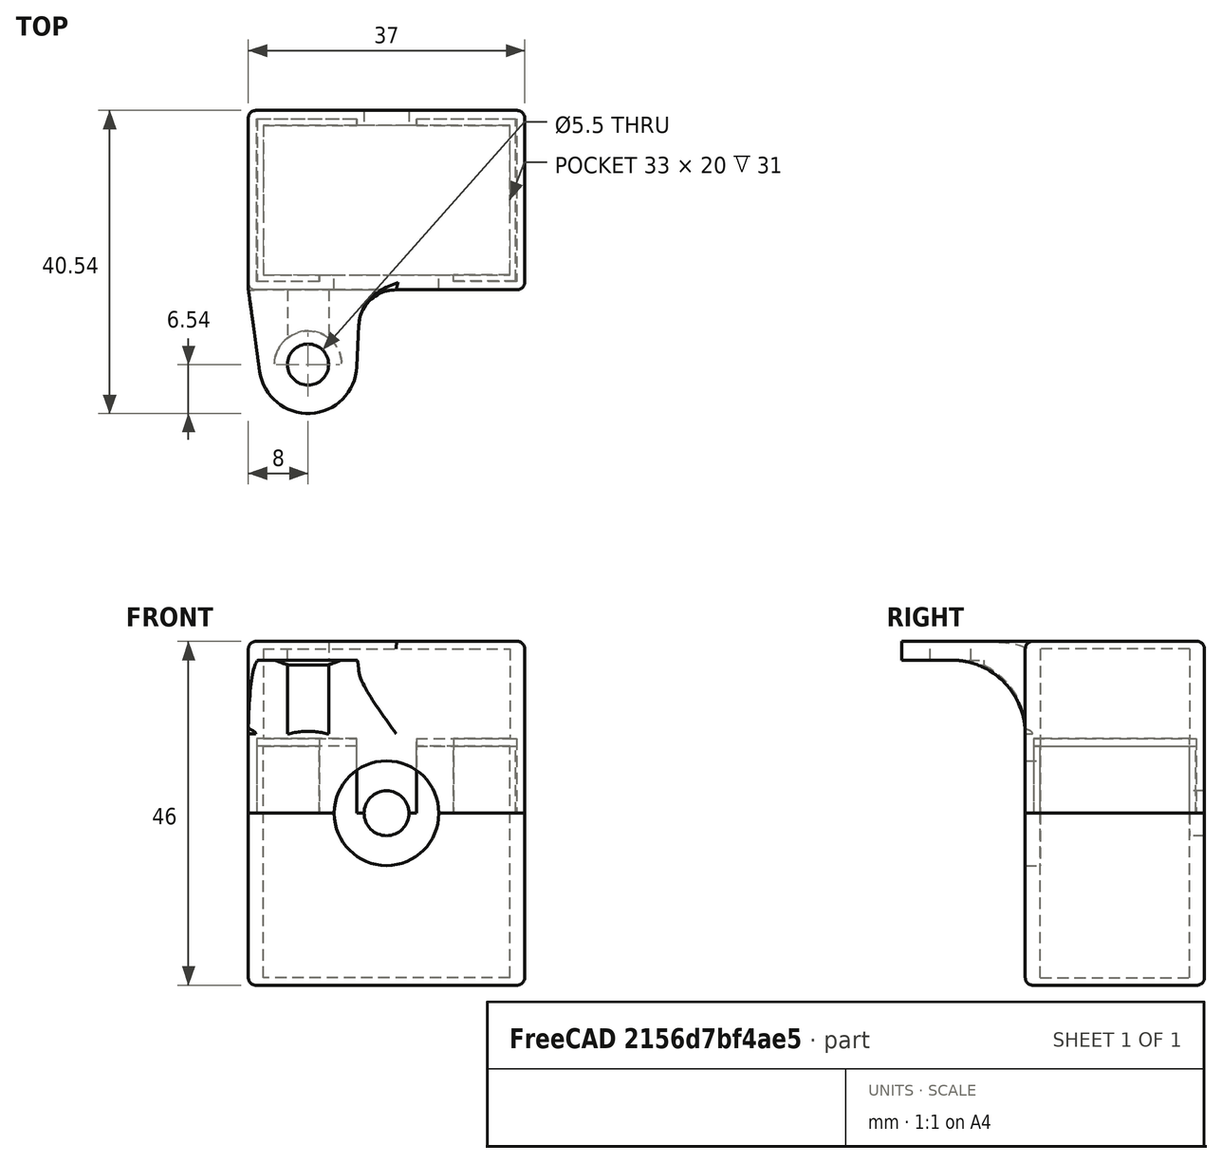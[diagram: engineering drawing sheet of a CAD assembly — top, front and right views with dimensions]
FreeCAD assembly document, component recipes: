
FREECAD ASSEMBLY — COMPONENT RECIPES ("logitech-quickcam-case")

This assembly document has 2 components, labeled P0..P1 below (a component is one placed body or linked part). 2 of them carry a construction recipe — the FreeCAD feature program that regenerates the part from scratch, quoted from this document or its linked companion documents; the rest are supplied as boundary geometry only. No exploded tour is included for this assembly.
COMPONENT P0 — recipe-attached ("free-side", modeled in this document).
Construction recipe (the document's own serialized feature program — sketch geometry with constraints, then the solid features built on it; lengths are millimeters unless a unit is written):

FEATURE [Sketcher::SketchObject] Sketch
  ArcFitTolerance = 1e-06
  AttachmentSupport = -> [Origin]
  ExternalTypes = [0]
  FullyConstrained = true
  MakeInternals = false
  MapMode = 5
  sketch-geometry (12):
    g0: LineSegment StartX=0 StartY=-24 StartZ=0 EndX=0 EndY=0 EndZ=0
    g1: LineSegment StartX=0 StartY=0 StartZ=0 EndX=37 EndY=0 EndZ=0
    g2: LineSegment StartX=37 StartY=0 StartZ=0 EndX=37 EndY=-24 EndZ=0
    g3: LineSegment StartX=37 StartY=-24 StartZ=0 EndX=0 EndY=-24 EndZ=0
    g4: LineSegment StartX=2 StartY=-22 StartZ=0 EndX=2 EndY=-2 EndZ=0
    g5: LineSegment StartX=2 StartY=-2 StartZ=0 EndX=35 EndY=-2 EndZ=0
    g6: LineSegment StartX=35 StartY=-2 StartZ=0 EndX=35 EndY=-22 EndZ=0
    g7: LineSegment StartX=35 StartY=-22 StartZ=0 EndX=2 EndY=-22 EndZ=0
    g8: LineSegment [constr] StartX=0 StartY=-2 StartZ=0 EndX=2 EndY=-2 EndZ=0
    g9: LineSegment [constr] StartX=35 StartY=-2 StartZ=0 EndX=37 EndY=-2 EndZ=0
    g10: LineSegment [constr] StartX=2 StartY=-22 StartZ=0 EndX=2 EndY=-24 EndZ=0
    g11: LineSegment [constr] StartX=2 StartY=-2 StartZ=0 EndX=2 EndY=0 EndZ=0
  constraints (36):
    c: Coincident(g0,g1)
    c: Coincident(g1,g2)
    c: Coincident(g2,g3)
    c: Coincident(g3,g0)
    c: Vertical(g0)
    c: Vertical(g2)
    c: Horizontal(g1)
    c: Horizontal(g3)
    c: PointOnObject(g0,g-2)
    c: PointOnObject(g1,g-1)
    c: Coincident(g4,g5)
    c: Coincident(g5,g6)
    c: Coincident(g6,g7)
    c: Coincident(g7,g4)
    c: Vertical(g4)
    c: Vertical(g6)
    c: Horizontal(g5)
    c: Horizontal(g7)
    c: PointOnObject(g8,g0)
    c: Coincident(g8,g4)
    c: Horizontal(g8)
    c: Coincident(g9,g5)
    c: PointOnObject(g9,g2)
    c: Horizontal(g9)
    c: Equal(g8,g9)
    c: Coincident(g10,g4)
    c: PointOnObject(g10,g3)
    c: Vertical(g10)
    c: Coincident(g11,g4)
    c: PointOnObject(g11,g1)
    c: Perpendicular(g11,g1)
    c: Equal(g11,g10)
    c: Equal(g11,g8)
    c: Distance(g4,g8) = 2
    c: DistanceY(g4,g4) = 20
    c: DistanceX(g7,g7) = 33
FEATURE [PartDesign::Pad] Pad
  Direction = (0,0,1)
  Length = 23
  Length2 = 10
  Profile = -> Sketch
  ReferenceAxis = -> Sketch [N_Axis]
  Refine = true
  SideType = 0
  Suppressed = false
  Type = 0
  Type2 = 0
FEATURE [Sketcher::SketchObject] Sketch001
  ArcFitTolerance = 1e-06
  AttachmentSupport = -> [Origin]
  ExternalTypes = [0]
  FullyConstrained = true
  MakeInternals = false
  MapMode = 5
  sketch-geometry (4):
    g0: LineSegment StartX=0 StartY=0 StartZ=0 EndX=0 EndY=-24 EndZ=0
    g1: LineSegment StartX=0 StartY=-24 StartZ=0 EndX=37 EndY=-24 EndZ=0
    g2: LineSegment StartX=37 StartY=-24 StartZ=0 EndX=37 EndY=0 EndZ=0
    g3: LineSegment StartX=37 StartY=0 StartZ=0 EndX=0 EndY=0 EndZ=0
  constraints (11):
    c: Coincident(g0,g1)
    c: Coincident(g1,g2)
    c: Coincident(g2,g3)
    c: Coincident(g3,g0)
    c: Vertical(g0)
    c: Vertical(g2)
    c: Horizontal(g1)
    c: Horizontal(g3)
    c: Distance(g0,g2) = 37
    c: Distance(g1,g3) = 24
    c: Coincident(g0,g-1)
FEATURE [PartDesign::Pad] Pad001
  BaseFeature = -> Pad
  Direction = (0,0,1)
  Length = 1
  Length2 = 10
  Profile = -> Sketch001
  ReferenceAxis = -> Sketch001 [N_Axis]
  Refine = true
  SideType = 0
  Suppressed = false
  Type = 0
  Type2 = 0
FEATURE [Sketcher::SketchObject] Sketch002
  ArcFitTolerance = 1e-06
  AttachmentSupport = -> [Origin]
  ExternalTypes = [0]
  FullyConstrained = true
  MakeInternals = false
  MapMode = 5
  sketch-geometry (28):
    g0: LineSegment StartX=1.2 StartY=-22.8 StartZ=0 EndX=1.2 EndY=-1.2 EndZ=0
    g1: LineSegment [constr] StartX=1.2 StartY=-1.2 StartZ=0 EndX=35.8 EndY=-1.2 EndZ=0
    g2: LineSegment StartX=35.8 StartY=-1.2 StartZ=0 EndX=35.8 EndY=-22.8 EndZ=0
    g3: LineSegment [constr] StartX=35.8 StartY=-22.8 StartZ=0 EndX=1.2 EndY=-22.8 EndZ=0
    g4: LineSegment StartX=2 StartY=-22 StartZ=0 EndX=2 EndY=-2 EndZ=0
    g5: LineSegment [constr] StartX=2 StartY=-2 StartZ=0 EndX=35 EndY=-2 EndZ=0
    g6: LineSegment StartX=35 StartY=-2 StartZ=0 EndX=35 EndY=-22 EndZ=0
    g7: LineSegment [constr] StartX=35 StartY=-22 StartZ=0 EndX=2 EndY=-22 EndZ=0
    g8: LineSegment [constr] StartX=1.2 StartY=-2 StartZ=0 EndX=2 EndY=-2 EndZ=0
    g9: LineSegment [constr] StartX=35 StartY=-2 StartZ=0 EndX=35.8 EndY=-2 EndZ=0
    g10: LineSegment [constr] StartX=2 StartY=-22 StartZ=0 EndX=2 EndY=-22.8 EndZ=0
    g11: LineSegment [constr] StartX=2 StartY=-2 StartZ=0 EndX=2 EndY=-1.2 EndZ=0
    g12: LineSegment [constr] StartX=1.2 StartY=-1.2 StartZ=0 EndX=0 EndY=-1.2 EndZ=0
    g13: LineSegment [constr] StartX=1.2 StartY=-1.2 StartZ=0 EndX=1.2 EndY=0 EndZ=0
    g14: LineSegment StartX=14.5 StartY=-2 StartZ=0 EndX=14.5 EndY=-1.2 EndZ=0
    g15: LineSegment StartX=22.5 StartY=-1.2 StartZ=0 EndX=22.5 EndY=-2 EndZ=0
    g16: LineSegment StartX=22.5 StartY=-1.2 StartZ=0 EndX=35.8 EndY=-1.2 EndZ=0
    g17: LineSegment StartX=35 StartY=-2 StartZ=0 EndX=22.5 EndY=-2 EndZ=0
    g18: LineSegment StartX=14.5 StartY=-2 StartZ=0 EndX=2 EndY=-2 EndZ=0
    g19: LineSegment StartX=14.5 StartY=-1.2 StartZ=0 EndX=2 EndY=-1.2 EndZ=0
    g20: LineSegment StartX=2 StartY=-1.2 StartZ=0 EndX=1.2 EndY=-1.2 EndZ=0
    g21: LineSegment StartX=2 StartY=-22 StartZ=0 EndX=9.5 EndY=-22 EndZ=0
    g22: LineSegment StartX=9.5 StartY=-22 StartZ=0 EndX=9.5 EndY=-22.8 EndZ=0
    g23: LineSegment StartX=9.5 StartY=-22.8 StartZ=0 EndX=1.2 EndY=-22.8 EndZ=0
    g24: LineSegment StartX=35 StartY=-22 StartZ=0 EndX=27.5 EndY=-22 EndZ=0
    g25: LineSegment StartX=27.5 StartY=-22 StartZ=0 EndX=27.5 EndY=-22.8 EndZ=0
    g26: LineSegment [constr] StartX=9.5 StartY=-22 StartZ=0 EndX=27.5 EndY=-22 EndZ=0
    g27: LineSegment StartX=27.5 StartY=-22.8 StartZ=0 EndX=35.8 EndY=-22.8 EndZ=0
  constraints (78):
    c: Coincident(g0,g1)
    c: Coincident(g1,g2)
    c: Coincident(g2,g3)
    c: Coincident(g3,g0)
    c: Vertical(g0)
    c: Vertical(g2)
    c: Horizontal(g1)
    c: Horizontal(g3)
    c: Coincident(g4,g5)
    c: Coincident(g5,g6)
    c: Coincident(g6,g7)
    c: Coincident(g7,g4)
    c: Vertical(g4)
    c: Vertical(g6)
    c: Horizontal(g5)
    c: Horizontal(g7)
    c: PointOnObject(g8,g0)
    c: Coincident(g8,g4)
    c: Horizontal(g8)
    c: Coincident(g9,g5)
    c: PointOnObject(g9,g2)
    c: Horizontal(g9)
    c: Equal(g8,g9)
    c: Coincident(g10,g4)
    c: PointOnObject(g10,g3)
    c: Vertical(g10)
    c: Coincident(g11,g4)
    c: PointOnObject(g11,g1)
    c: Perpendicular(g11,g1)
    c: Equal(g11,g10)
    c: Equal(g11,g8)
    c: Distance(g4,g8) = 0.8
    c: DistanceY(g4,g4) = 20
    c: DistanceX(g7,g7) = 33
    c: Coincident(g12,g0)
    c: PointOnObject(g12,g-2)
    c: Horizontal(g12)
    c: Coincident(g13,g0)
    c: Vertical(g13)
    c: Equal(g12,g13)
    c: PointOnObject(g13,g-1)
    c: DistanceY(g13,g13) = 1.2
    c: PointOnObject(g14,g5)
    c: PointOnObject(g14,g1)
    c: PointOnObject(g15,g1)
    c: PointOnObject(g15,g5)
    c: Vertical(g15)
    c: Coincident(g16,g15)
    c: Coincident(g16,g1)
    c: Coincident(g17,g5)
    c: Coincident(g17,g15)
    c: Coincident(g18,g14)
    c: Coincident(g18,g4)
    c: Coincident(g19,g14)
    c: Coincident(g19,g11)
    c: Perpendicular(g18,g14)
    c: DistanceX(g14,g15) = 8
    c: Coincident(g20,g11)
    c: Coincident(g20,g0)
    c: Coincident(g21,g4)
    c: Coincident(g21,g22)
    c: Vertical(g22)
    c: Coincident(g22,g23)
    c: Coincident(g23,g0)
    c: Coincident(g24,g6)
    c: Coincident(g24,g25)
    c: Coincident(g26,g21)
    c: Coincident(g26,g24)
    c: Horizontal(g26)
    c: DistanceX(g26,g26) = 18
    c: Perpendicular(g25,g24)
    c: Perpendicular(g6,g24)
    c: Horizontal(g25,g22)
    c: Horizontal(g22,g2)
    c: Equal(g18,g17)
    c: Equal(g21,g24)
    c: Coincident(g27,g25)
    c: Coincident(g27,g2)
FEATURE [Part::DatumPlane] DatumPlane
  AttachmentOffset = pos=(0,0,0) rot=(0,1,0;1.5708rad)
  AttachmentSupport = -> [Pad001]
  MapMode = 7
  Placement = pos=(2,-2,23) rot=(1,0,0;1.5708rad)
FEATURE [Sketcher::SketchObject] Sketch003
  ArcFitTolerance = 1e-06
  AttachmentSupport = -> [DatumPlane]
  ExternalTypes = [0]
  FullyConstrained = true
  MakeInternals = false
  MapMode = 5
  Placement = pos=(2,-2,23) rot=(1,0,0;1.5708rad)
  sketch-geometry (1):
    g0: Circle CenterX=16.5 CenterY=0 CenterZ=0 NormalX=0 NormalY=0 NormalZ=1 AngleXU=0 Radius=3
  constraints (3):
    c: PointOnObject(g0,g-1)
    c: Diameter(g0) = 6
    c: DistanceX(g-1,g0) = 16.5
FEATURE [PartDesign::Pocket] Pocket
  BaseFeature = -> Pad001
  Direction = (0,1,-2e-16)
  Length = 5
  Length2 = 5
  Profile = -> Sketch003
  ReferenceAxis = -> Sketch003 [N_Axis]
  Refine = true
  SideType = 2
  Suppressed = false
  Type = 0
  Type2 = 0
FEATURE [Part::DatumPlane] DatumPlane001
  AttachmentOffset = pos=(0,0,0) rot=(0,1,0;1.5708rad)
  AttachmentSupport = -> [Pad001]
  MapMode = 7
  Placement = pos=(35,-22,23) rot=(0,0.707107,0.707107;3.14159rad)
FEATURE [Sketcher::SketchObject] Sketch005
  ArcFitTolerance = 1e-06
  AttachmentSupport = -> [DatumPlane001]
  ExternalTypes = [0]
  FullyConstrained = true
  MakeInternals = false
  MapMode = 5
  Placement = pos=(35,-22,23) rot=(0,0.707107,0.707107;3.14159rad)
  sketch-geometry (1):
    g0: Circle CenterX=16.5 CenterY=0 CenterZ=0 NormalX=0 NormalY=0 NormalZ=1 AngleXU=0 Radius=7
  constraints (3):
    c: Diameter(g0) = 14
    c: PointOnObject(g0,g-1)
    c: DistanceX(g-1,g0) = 16.5
FEATURE [PartDesign::Pocket] Pocket001
  BaseFeature = -> Pocket
  Direction = (0,-1,2e-16)
  Length = 5
  Length2 = 5
  Profile = -> Sketch005
  ReferenceAxis = -> Sketch005 [N_Axis]
  Refine = true
  SideType = 2
  Suppressed = false
  Type = 0
  Type2 = 0
FEATURE [PartDesign::Pad] Pad002
  BaseFeature = -> Pocket001
  Direction = (0,0,1)
  Length = 32
  Length2 = 10
  Profile = -> Sketch002
  ReferenceAxis = -> Sketch002 [N_Axis]
  Refine = true
  SideType = 0
  Suppressed = false
  Type = 0
  Type2 = 0
FEATURE [PartDesign::Fillet] Fillet002
  Base = -> Pad002 [Edge29,Edge27,Edge28,Edge25,Edge49,Edge46,Edge26,Edge48]
  BaseFeature = -> Pad002
  Radius = 0.999
  Refine = true
  SupportTransform = false
  Suppressed = false
  UseAllEdges = false
FEATURE [PartDesign::Body] Body  label="free-side"
  AllowCompound = false
  Group = -> [Sketch,Pad,Sketch001,Pad001,Sketch003,Pocket,Sketch002,Sketch005,Pocket001,Pad002,DatumPlane,DatumPlane001,Fillet002]
  Origin = -> Origin
  Tip = -> Fillet002
COMPONENT P1 — recipe-attached ("bracket-side", modeled in this document).
Construction recipe (the document's own serialized feature program — sketch geometry with constraints, then the solid features built on it; lengths are millimeters unless a unit is written):

FEATURE [Sketcher::SketchObject] Sketch006
  ArcFitTolerance = 1e-06
  AttachmentOffset = pos=(0,0,0) rot=(1,0,0;3.14159rad)
  ExternalTypes = [0]
  FullyConstrained = true
  MakeInternals = false
  MapMode = 5
  Placement = pos=(0,0,23) rot=(0,0,1;0rad)
  sketch-geometry (28):
    g0: LineSegment StartX=1.1 StartY=-22.9 StartZ=0 EndX=1.1 EndY=-1.1 EndZ=0
    g1: LineSegment [constr] StartX=1.1 StartY=-1.1 StartZ=0 EndX=35.9 EndY=-1.1 EndZ=0
    g2: LineSegment StartX=35.9 StartY=-1.1 StartZ=0 EndX=35.9 EndY=-22.9 EndZ=0
    g3: LineSegment [constr] StartX=35.9 StartY=-22.9 StartZ=0 EndX=1.1 EndY=-22.9 EndZ=0
    g4: LineSegment StartX=2 StartY=-22 StartZ=0 EndX=2 EndY=-2 EndZ=0
    g5: LineSegment [constr] StartX=2 StartY=-2 StartZ=0 EndX=35 EndY=-2 EndZ=0
    g6: LineSegment StartX=35 StartY=-2 StartZ=0 EndX=35 EndY=-22 EndZ=0
    g7: LineSegment [constr] StartX=35 StartY=-22 StartZ=0 EndX=2 EndY=-22 EndZ=0
    g8: LineSegment [constr] StartX=1.1 StartY=-2 StartZ=0 EndX=2 EndY=-2 EndZ=0
    g9: LineSegment [constr] StartX=35 StartY=-2 StartZ=0 EndX=35.9 EndY=-2 EndZ=0
    g10: LineSegment [constr] StartX=2 StartY=-22 StartZ=0 EndX=2 EndY=-22.9 EndZ=0
    g11: LineSegment [constr] StartX=2 StartY=-2 StartZ=0 EndX=2 EndY=-1.1 EndZ=0
    g12: LineSegment [constr] StartX=1.1 StartY=-1.1 StartZ=0 EndX=0 EndY=-1.1 EndZ=0
    g13: LineSegment [constr] StartX=1.1 StartY=-1.1 StartZ=0 EndX=1.1 EndY=0 EndZ=0
    g14: LineSegment StartX=14.5 StartY=-2 StartZ=0 EndX=14.5 EndY=-1.1 EndZ=0
    g15: LineSegment StartX=22.5 StartY=-1.1 StartZ=0 EndX=22.5 EndY=-2 EndZ=0
    g16: LineSegment StartX=22.5 StartY=-1.1 StartZ=0 EndX=35.9 EndY=-1.1 EndZ=0
    g17: LineSegment StartX=35 StartY=-2 StartZ=0 EndX=22.5 EndY=-2 EndZ=0
    g18: LineSegment StartX=14.5 StartY=-2 StartZ=0 EndX=2 EndY=-2 EndZ=0
    g19: LineSegment StartX=14.5 StartY=-1.1 StartZ=0 EndX=2 EndY=-1.1 EndZ=0
    g20: LineSegment StartX=2 StartY=-1.1 StartZ=0 EndX=1.1 EndY=-1.1 EndZ=0
    g21: LineSegment StartX=2 StartY=-22 StartZ=0 EndX=9.5 EndY=-22 EndZ=0
    g22: LineSegment StartX=9.5 StartY=-22 StartZ=0 EndX=9.5 EndY=-22.9 EndZ=0
    g23: LineSegment StartX=9.5 StartY=-22.9 StartZ=0 EndX=1.1 EndY=-22.9 EndZ=0
    g24: LineSegment StartX=35 StartY=-22 StartZ=0 EndX=27.5 EndY=-22 EndZ=0
    g25: LineSegment StartX=27.5 StartY=-22 StartZ=0 EndX=27.5 EndY=-22.9 EndZ=0
    g26: LineSegment [constr] StartX=9.5 StartY=-22 StartZ=0 EndX=27.5 EndY=-22 EndZ=0
    g27: LineSegment StartX=27.5 StartY=-22.9 StartZ=0 EndX=35.9 EndY=-22.9 EndZ=0
  constraints (78):
    c: Coincident(g0,g1)
    c: Coincident(g1,g2)
    c: Coincident(g2,g3)
    c: Coincident(g3,g0)
    c: Vertical(g0)
    c: Vertical(g2)
    c: Horizontal(g1)
    c: Horizontal(g3)
    c: Coincident(g4,g5)
    c: Coincident(g5,g6)
    c: Coincident(g6,g7)
    c: Coincident(g7,g4)
    c: Vertical(g4)
    c: Vertical(g6)
    c: Horizontal(g5)
    c: Horizontal(g7)
    c: PointOnObject(g8,g0)
    c: Coincident(g8,g4)
    c: Horizontal(g8)
    c: Coincident(g9,g5)
    c: PointOnObject(g9,g2)
    c: Horizontal(g9)
    c: Equal(g8,g9)
    c: Coincident(g10,g4)
    c: PointOnObject(g10,g3)
    c: Vertical(g10)
    c: Coincident(g11,g4)
    c: PointOnObject(g11,g1)
    c: Perpendicular(g11,g1)
    c: Equal(g11,g10)
    c: Equal(g11,g8)
    c: Distance(g4,g8) = 0.9
    c: DistanceY(g4,g4) = 20
    c: DistanceX(g7,g7) = 33
    c: Coincident(g12,g0)
    c: PointOnObject(g12,g-2)
    c: Horizontal(g12)
    c: Coincident(g13,g0)
    c: Vertical(g13)
    c: Equal(g12,g13)
    c: PointOnObject(g13,g-1)
    c: DistanceY(g13,g13) = 1.1
    c: PointOnObject(g14,g5)
    c: PointOnObject(g14,g1)
    c: PointOnObject(g15,g1)
    c: PointOnObject(g15,g5)
    c: Vertical(g15)
    c: Coincident(g16,g15)
    c: Coincident(g16,g1)
    c: Coincident(g17,g5)
    c: Coincident(g17,g15)
    c: Coincident(g18,g14)
    c: Coincident(g18,g4)
    c: Coincident(g19,g14)
    c: Coincident(g19,g11)
    c: Perpendicular(g18,g14)
    c: DistanceX(g14,g15) = 8
    c: Coincident(g20,g11)
    c: Coincident(g20,g0)
    c: Coincident(g21,g4)
    c: Coincident(g21,g22)
    c: Vertical(g22)
    c: Coincident(g22,g23)
    c: Coincident(g23,g0)
    c: Coincident(g24,g6)
    c: Coincident(g24,g25)
    c: Coincident(g26,g21)
    c: Coincident(g26,g24)
    c: Horizontal(g26)
    c: DistanceX(g26,g26) = 18
    c: Perpendicular(g25,g24)
    c: Perpendicular(g6,g24)
    c: Horizontal(g25,g22)
    c: Horizontal(g22,g2)
    c: Equal(g18,g17)
    c: Equal(g21,g24)
    c: Coincident(g27,g25)
    c: Coincident(g27,g2)
FEATURE [Sketcher::SketchObject] Sketch007
  ArcFitTolerance = 1e-06
  AttachmentSupport = -> [Origin006]
  ExternalTypes = [0]
  FullyConstrained = true
  MakeInternals = false
  MapMode = 5
  sketch-geometry (12):
    g0: LineSegment StartX=0 StartY=-24 StartZ=0 EndX=0 EndY=0 EndZ=0
    g1: LineSegment StartX=0 StartY=0 StartZ=0 EndX=37 EndY=0 EndZ=0
    g2: LineSegment StartX=37 StartY=0 StartZ=0 EndX=37 EndY=-24 EndZ=0
    g3: LineSegment StartX=37 StartY=-24 StartZ=0 EndX=0 EndY=-24 EndZ=0
    g4: LineSegment StartX=2 StartY=-22 StartZ=0 EndX=2 EndY=-2 EndZ=0
    g5: LineSegment StartX=2 StartY=-2 StartZ=0 EndX=35 EndY=-2 EndZ=0
    g6: LineSegment StartX=35 StartY=-2 StartZ=0 EndX=35 EndY=-22 EndZ=0
    g7: LineSegment StartX=35 StartY=-22 StartZ=0 EndX=2 EndY=-22 EndZ=0
    g8: LineSegment [constr] StartX=0 StartY=-2 StartZ=0 EndX=2 EndY=-2 EndZ=0
    g9: LineSegment [constr] StartX=35 StartY=-2 StartZ=0 EndX=37 EndY=-2 EndZ=0
    g10: LineSegment [constr] StartX=2 StartY=-22 StartZ=0 EndX=2 EndY=-24 EndZ=0
    g11: LineSegment [constr] StartX=2 StartY=-2 StartZ=0 EndX=2 EndY=0 EndZ=0
  constraints (36):
    c: Coincident(g0,g1)
    c: Coincident(g1,g2)
    c: Coincident(g2,g3)
    c: Coincident(g3,g0)
    c: Vertical(g0)
    c: Vertical(g2)
    c: Horizontal(g1)
    c: Horizontal(g3)
    c: PointOnObject(g0,g-2)
    c: PointOnObject(g1,g-1)
    c: Coincident(g4,g5)
    c: Coincident(g5,g6)
    c: Coincident(g6,g7)
    c: Coincident(g7,g4)
    c: Vertical(g4)
    c: Vertical(g6)
    c: Horizontal(g5)
    c: Horizontal(g7)
    c: PointOnObject(g8,g0)
    c: Coincident(g8,g4)
    c: Horizontal(g8)
    c: Coincident(g9,g5)
    c: PointOnObject(g9,g2)
    c: Horizontal(g9)
    c: Equal(g8,g9)
    c: Coincident(g10,g4)
    c: PointOnObject(g10,g3)
    c: Vertical(g10)
    c: Coincident(g11,g4)
    c: PointOnObject(g11,g1)
    c: Perpendicular(g11,g1)
    c: Equal(g11,g10)
    c: Equal(g11,g8)
    c: Distance(g4,g8) = 2
    c: DistanceY(g4,g4) = 20
    c: DistanceX(g7,g7) = 33
FEATURE [PartDesign::Pad] Pad003
  Direction = (0,0,1)
  Length = 23
  Length2 = 10
  Profile = -> Sketch007
  ReferenceAxis = -> Sketch007 [N_Axis]
  Refine = true
  SideType = 0
  Suppressed = false
  Type = 0
  Type2 = 0
FEATURE [Sketcher::SketchObject] Sketch008
  ArcFitTolerance = 1e-06
  AttachmentSupport = -> [Origin006]
  ExternalTypes = [0]
  FullyConstrained = true
  MakeInternals = false
  MapMode = 5
  sketch-geometry (4):
    g0: LineSegment StartX=0 StartY=0 StartZ=0 EndX=0 EndY=-24 EndZ=0
    g1: LineSegment StartX=0 StartY=-24 StartZ=0 EndX=37 EndY=-24 EndZ=0
    g2: LineSegment StartX=37 StartY=-24 StartZ=0 EndX=37 EndY=0 EndZ=0
    g3: LineSegment StartX=37 StartY=0 StartZ=0 EndX=0 EndY=0 EndZ=0
  constraints (11):
    c: Coincident(g0,g1)
    c: Coincident(g1,g2)
    c: Coincident(g2,g3)
    c: Coincident(g3,g0)
    c: Vertical(g0)
    c: Vertical(g2)
    c: Horizontal(g1)
    c: Horizontal(g3)
    c: Distance(g0,g2) = 37
    c: Distance(g1,g3) = 24
    c: Coincident(g0,g-1)
FEATURE [PartDesign::Pad] Pad004
  BaseFeature = -> Pad003
  Direction = (0,0,1)
  Length = 1
  Length2 = 10
  Profile = -> Sketch008
  ReferenceAxis = -> Sketch008 [N_Axis]
  Refine = true
  SideType = 0
  Suppressed = false
  Type = 0
  Type2 = 0
FEATURE [Part::DatumPlane] DatumPlane002
  AttachmentOffset = pos=(0,0,0) rot=(0,1,0;1.5708rad)
  AttachmentSupport = -> [Pad004]
  MapMode = 7
  Placement = pos=(2,-2,23) rot=(1,0,0;1.5708rad)
FEATURE [Part::DatumPlane] DatumPlane003
  AttachmentOffset = pos=(0,0,0) rot=(0,1,0;1.5708rad)
  AttachmentSupport = -> [Pad004]
  MapMode = 7
  Placement = pos=(35,-22,23) rot=(0,0.707107,0.707107;3.14159rad)
FEATURE [Sketcher::SketchObject] Sketch009
  ArcFitTolerance = 1e-06
  AttachmentSupport = -> [Origin006]
  ExternalTypes = [0]
  FullyConstrained = true
  MakeInternals = false
  MapMode = 5
  sketch-geometry (28):
    g0: LineSegment StartX=1.2 StartY=-22.8 StartZ=0 EndX=1.2 EndY=-1.2 EndZ=0
    g1: LineSegment [constr] StartX=1.2 StartY=-1.2 StartZ=0 EndX=35.8 EndY=-1.2 EndZ=0
    g2: LineSegment StartX=35.8 StartY=-1.2 StartZ=0 EndX=35.8 EndY=-22.8 EndZ=0
    g3: LineSegment [constr] StartX=35.8 StartY=-22.8 StartZ=0 EndX=1.2 EndY=-22.8 EndZ=0
    g4: LineSegment StartX=2 StartY=-22 StartZ=0 EndX=2 EndY=-2 EndZ=0
    g5: LineSegment [constr] StartX=2 StartY=-2 StartZ=0 EndX=35 EndY=-2 EndZ=0
    g6: LineSegment StartX=35 StartY=-2 StartZ=0 EndX=35 EndY=-22 EndZ=0
    g7: LineSegment [constr] StartX=35 StartY=-22 StartZ=0 EndX=2 EndY=-22 EndZ=0
    g8: LineSegment [constr] StartX=1.2 StartY=-2 StartZ=0 EndX=2 EndY=-2 EndZ=0
    g9: LineSegment [constr] StartX=35 StartY=-2 StartZ=0 EndX=35.8 EndY=-2 EndZ=0
    g10: LineSegment [constr] StartX=2 StartY=-22 StartZ=0 EndX=2 EndY=-22.8 EndZ=0
    g11: LineSegment [constr] StartX=2 StartY=-2 StartZ=0 EndX=2 EndY=-1.2 EndZ=0
    g12: LineSegment [constr] StartX=1.2 StartY=-1.2 StartZ=0 EndX=0 EndY=-1.2 EndZ=0
    g13: LineSegment [constr] StartX=1.2 StartY=-1.2 StartZ=0 EndX=1.2 EndY=0 EndZ=0
    g14: LineSegment StartX=14.5 StartY=-2 StartZ=0 EndX=14.5 EndY=-1.2 EndZ=0
    g15: LineSegment StartX=22.5 StartY=-1.2 StartZ=0 EndX=22.5 EndY=-2 EndZ=0
    g16: LineSegment StartX=22.5 StartY=-1.2 StartZ=0 EndX=35.8 EndY=-1.2 EndZ=0
    g17: LineSegment StartX=35 StartY=-2 StartZ=0 EndX=22.5 EndY=-2 EndZ=0
    g18: LineSegment StartX=14.5 StartY=-2 StartZ=0 EndX=2 EndY=-2 EndZ=0
    g19: LineSegment StartX=14.5 StartY=-1.2 StartZ=0 EndX=2 EndY=-1.2 EndZ=0
    g20: LineSegment StartX=2 StartY=-1.2 StartZ=0 EndX=1.2 EndY=-1.2 EndZ=0
    g21: LineSegment StartX=2 StartY=-22 StartZ=0 EndX=9.5 EndY=-22 EndZ=0
    g22: LineSegment StartX=9.5 StartY=-22 StartZ=0 EndX=9.5 EndY=-22.8 EndZ=0
    g23: LineSegment StartX=9.5 StartY=-22.8 StartZ=0 EndX=1.2 EndY=-22.8 EndZ=0
    g24: LineSegment StartX=35 StartY=-22 StartZ=0 EndX=27.5 EndY=-22 EndZ=0
    g25: LineSegment StartX=27.5 StartY=-22 StartZ=0 EndX=27.5 EndY=-22.8 EndZ=0
    g26: LineSegment [constr] StartX=9.5 StartY=-22 StartZ=0 EndX=27.5 EndY=-22 EndZ=0
    g27: LineSegment StartX=27.5 StartY=-22.8 StartZ=0 EndX=35.8 EndY=-22.8 EndZ=0
  constraints (78):
    c: Coincident(g0,g1)
    c: Coincident(g1,g2)
    c: Coincident(g2,g3)
    c: Coincident(g3,g0)
    c: Vertical(g0)
    c: Vertical(g2)
    c: Horizontal(g1)
    c: Horizontal(g3)
    c: Coincident(g4,g5)
    c: Coincident(g5,g6)
    c: Coincident(g6,g7)
    c: Coincident(g7,g4)
    c: Vertical(g4)
    c: Vertical(g6)
    c: Horizontal(g5)
    c: Horizontal(g7)
    c: PointOnObject(g8,g0)
    c: Coincident(g8,g4)
    c: Horizontal(g8)
    c: Coincident(g9,g5)
    c: PointOnObject(g9,g2)
    c: Horizontal(g9)
    c: Equal(g8,g9)
    c: Coincident(g10,g4)
    c: PointOnObject(g10,g3)
    c: Vertical(g10)
    c: Coincident(g11,g4)
    c: PointOnObject(g11,g1)
    c: Perpendicular(g11,g1)
    c: Equal(g11,g10)
    c: Equal(g11,g8)
    c: Distance(g4,g8) = 0.8
    c: DistanceY(g4,g4) = 20
    c: DistanceX(g7,g7) = 33
    c: Coincident(g12,g0)
    c: PointOnObject(g12,g-2)
    c: Horizontal(g12)
    c: Coincident(g13,g0)
    c: Vertical(g13)
    c: Equal(g12,g13)
    c: PointOnObject(g13,g-1)
    c: DistanceY(g13,g13) = 1.2
    c: PointOnObject(g14,g5)
    c: PointOnObject(g14,g1)
    c: PointOnObject(g15,g1)
    c: PointOnObject(g15,g5)
    c: Vertical(g15)
    c: Coincident(g16,g15)
    c: Coincident(g16,g1)
    c: Coincident(g17,g5)
    c: Coincident(g17,g15)
    c: Coincident(g18,g14)
    c: Coincident(g18,g4)
    c: Coincident(g19,g14)
    c: Coincident(g19,g11)
    c: Perpendicular(g18,g14)
    c: DistanceX(g14,g15) = 8
    c: Coincident(g20,g11)
    c: Coincident(g20,g0)
    c: Coincident(g21,g4)
    c: Coincident(g21,g22)
    c: Vertical(g22)
    c: Coincident(g22,g23)
    c: Coincident(g23,g0)
    c: Coincident(g24,g6)
    c: Coincident(g24,g25)
    c: Coincident(g26,g21)
    c: Coincident(g26,g24)
    c: Horizontal(g26)
    c: DistanceX(g26,g26) = 18
    c: Perpendicular(g25,g24)
    c: Perpendicular(g6,g24)
    c: Horizontal(g25,g22)
    c: Horizontal(g22,g2)
    c: Equal(g18,g17)
    c: Equal(g21,g24)
    c: Coincident(g27,g25)
    c: Coincident(g27,g2)
FEATURE [Sketcher::SketchObject] Sketch010
  ArcFitTolerance = 1e-06
  AttachmentSupport = -> [DatumPlane002]
  ExternalTypes = [0]
  FullyConstrained = true
  MakeInternals = false
  MapMode = 5
  Placement = pos=(2,-2,23) rot=(1,0,0;1.5708rad)
  sketch-geometry (1):
    g0: Circle CenterX=16.5 CenterY=0 CenterZ=0 NormalX=0 NormalY=0 NormalZ=1 AngleXU=0 Radius=3
  constraints (3):
    c: PointOnObject(g0,g-1)
    c: Diameter(g0) = 6
    c: DistanceX(g-1,g0) = 16.5
FEATURE [PartDesign::Pocket] Pocket002
  BaseFeature = -> Pad004
  Direction = (0,1,-2e-16)
  Length = 5
  Length2 = 5
  Profile = -> Sketch010
  ReferenceAxis = -> Sketch010 [N_Axis]
  Refine = true
  SideType = 2
  Suppressed = false
  Type = 0
  Type2 = 0
FEATURE [Sketcher::SketchObject] Sketch011
  ArcFitTolerance = 1e-06
  AttachmentSupport = -> [DatumPlane003]
  ExternalTypes = [0]
  FullyConstrained = true
  MakeInternals = false
  MapMode = 5
  Placement = pos=(35,-22,23) rot=(0,0.707107,0.707107;3.14159rad)
  sketch-geometry (1):
    g0: Circle CenterX=16.5 CenterY=0 CenterZ=0 NormalX=0 NormalY=0 NormalZ=1 AngleXU=0 Radius=7
  constraints (3):
    c: Diameter(g0) = 14
    c: PointOnObject(g0,g-1)
    c: DistanceX(g-1,g0) = 16.5
FEATURE [PartDesign::Pocket] Pocket003
  BaseFeature = -> Pocket002
  Direction = (0,-1,2e-16)
  Length = 5
  Length2 = 5
  Profile = -> Sketch011
  ReferenceAxis = -> Sketch011 [N_Axis]
  Refine = true
  SideType = 2
  Suppressed = false
  Type = 0
  Type2 = 0
FEATURE [PartDesign::Pad] Pad005
  BaseFeature = -> Pocket003
  Direction = (0,0,1)
  Length = 27
  Length2 = 10
  Profile = -> Sketch009
  ReferenceAxis = -> Sketch009 [N_Axis]
  Refine = true
  SideType = 0
  Suppressed = false
  Type = 0
  Type2 = 0
FEATURE [PartDesign::Pocket] Pocket004
  BaseFeature = -> Pad005
  Direction = (0,0,-1)
  Length = 10
  Length2 = 5
  Profile = -> Sketch006
  ReferenceAxis = -> Sketch006 [N_Axis]
  Refine = true
  SideType = 2
  Suppressed = false
  Type = 0
  Type2 = 0
FEATURE [Part::DatumPlane] DatumPlane005
  AttachmentOffset = pos=(0,0,0) rot=(-0.57735,0.57735,0.57735;2.0944rad)
  AttachmentSupport = -> [Pocket004]
  MapMode = 7
  Placement = pos=(37,-24,0) rot=(0,0,1;3.14159rad)
FEATURE [Sketcher::SketchObject] Sketch013
  ArcFitTolerance = 1e-06
  AttachmentSupport = -> [DatumPlane005]
  ExternalTypes = [0]
  FullyConstrained = true
  MakeInternals = false
  MapMode = 5
  Placement = pos=(37,-24,0) rot=(0,0,1;3.14159rad)
  sketch-geometry (7):
    g0: ArcOfCircle CenterX=8 CenterY=10 CenterZ=0 NormalX=0 NormalY=0 NormalZ=1 AngleXU=0 Radius=6.53503 StartAngle=0.0457794 EndAngle=3.00239
    g1: Circle CenterX=8 CenterY=10 CenterZ=0 NormalX=0 NormalY=0 NormalZ=1 AngleXU=0 Radius=2.75
    g2: LineSegment StartX=1.52819 StartY=10.9068 StartZ=0 EndX=-2e-16 EndY=0 EndZ=0
    g3: LineSegment StartX=14.5282 StartY=10.2991 StartZ=0 EndX=15 EndY=0 EndZ=0
    g4: LineSegment StartX=-2e-16 StartY=0 StartZ=0 EndX=15 EndY=0 EndZ=0
    g5: LineSegment [constr] StartX=1.52819 StartY=10.9068 StartZ=0 EndX=11.304 EndY=80.6778 EndZ=0
    g6: LineSegment [constr] StartX=14.5282 StartY=10.2991 StartZ=0 EndX=11.304 EndY=80.6778 EndZ=0
  constraints (17):
    c: Coincident(g1,g0)
    c: Diameter(g1) = 5.5
    c: DistanceX(g0,g0) = 13
    c: Coincident(g2,g0)
    c: Coincident(g3,g0)
    c: PointOnObject(g3,g-1)
    c: Coincident(g4,g2)
    c: Coincident(g4,g3)
    c: Distance(g0,g-2) = 8
    c: Coincident(g2,g-1)
    c: Distance(g0,g-1) = 10
    c: Tangent(g6,g0) = -1.5708
    c: Parallel(g6,g3)
    c: Parallel(g2,g5)
    c: Tangent(g5,g0) = 1.5708
    c: DistanceX(g4,g4) = 15
    c: Coincident(g5,g6)
FEATURE [PartDesign::Pad] Pad006
  BaseFeature = -> Pocket004
  Direction = (0,0,1)
  Length = 2.5
  Length2 = 10
  Profile = -> Sketch013
  ReferenceAxis = -> Sketch013 [N_Axis]
  Refine = true
  SideType = 0
  Suppressed = false
  Type = 0
  Type2 = 0
FEATURE [PartDesign::Fillet] Fillet
  Base = -> Pad006 [Edge70]
  BaseFeature = -> Pad006
  Radius = 9.9
  Refine = true
  SupportTransform = false
  Suppressed = false
  UseAllEdges = false
FEATURE [PartDesign::Fillet] Fillet003
  Base = -> Fillet [Edge1,Edge16,Edge15,Edge51,Edge11,Edge9,Edge50,Edge49]
  BaseFeature = -> Fillet
  Radius = 1
  Refine = true
  SupportTransform = false
  Suppressed = false
  UseAllEdges = false
FEATURE [PartDesign::Fillet] Fillet004
  Base = -> Fillet003 [Edge7]
  BaseFeature = -> Fillet003
  Radius = 5
  Refine = true
  SupportTransform = false
  Suppressed = false
  UseAllEdges = false
FEATURE [Sketcher::SketchObject] Sketch014
  ArcFitTolerance = 1e-06
  AttachmentOffset = pos=(0,0,2.5) rot=(0,0,1;0rad)
  AttachmentSupport = -> [DatumPlane005]
  ExternalTypes = [0]
  FullyConstrained = true
  MakeInternals = false
  MapMode = 5
  Placement = pos=(37,-24,2.5) rot=(0,0,1;3.14159rad)
  sketch-geometry (1):
    g0: Circle CenterX=8 CenterY=10 CenterZ=0 NormalX=0 NormalY=0 NormalZ=1 AngleXU=0 Radius=4.5
  constraints (3):
    c: Distance(g0,g-1) = 10
    c: DistanceX(g-1,g0) = 8
    c: Diameter(g0) = 9
FEATURE [PartDesign::Pocket] Pocket005
  BaseFeature = -> Fillet004
  Direction = (0,0,-1)
  Length = 5
  Length2 = 5
  Profile = -> Sketch014
  ReferenceAxis = -> Sketch014 [N_Axis]
  Refine = true
  Reversed = true
  SideType = 0
  Suppressed = false
  Type = 0
  Type2 = 0
FEATURE [PartDesign::Body] Body001  label="bracket-side"
  AllowCompound = false
  Group = -> [Sketch007,Pad003,Sketch008,Pad004,Sketch010,Pocket002,Sketch009,Sketch011,Pocket003,Pad005,DatumPlane002,DatumPlane003,Sketch006,Pocket004,Sketch013,Pad006,DatumPlane005,Fillet,Fillet003,Fillet004,Sketch014,Pocket005]
  Origin = -> Origin006
  Placement = pos=(37,1.8e-15,46) rot=(0,1,0;3.14159rad)
  Tip = -> Pocket005
PROVENANCE & LICENSES
A FreeCAD (.FCStd) document from a public repository crawl; recipes are the document's own serialized feature recipes (and, for linked parts, companion documents' recipes).
License: cc-by-sa-4.0.
